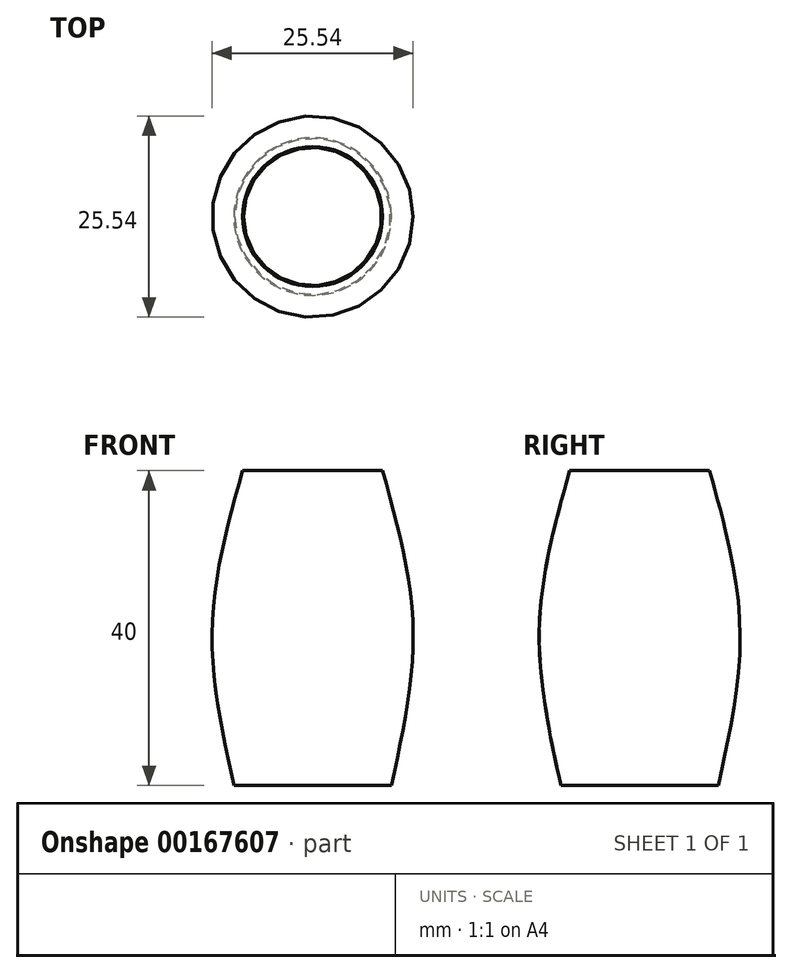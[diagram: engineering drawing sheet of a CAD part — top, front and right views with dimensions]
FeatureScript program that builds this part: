
annotation { "Feature Type Name" : "Feature", "Feature Type Description" : "" }
export const myFeature = defineFeature(function(context is Context, id is Id, definition is map)
    precondition{}
    {
        {
            var Q0;
            Q0=qCreatedBy(makeId("Top.planeOp"),FACE);
            cPlane(context, id + "F0", {"entities" : qUnion([Q0]), "cplaneType" : CPlaneType.OFFSET, "offset" : 20 * mm, "width" : 152.4 * mm, "height" : 152.4 * mm});
        }
        {
            var Q0;
            Q0=qCreatedBy(id+"F0.planeOp",FACE);
            cPlane(context, id + "F1", {"entities" : qUnion([Q0]), "cplaneType" : CPlaneType.OFFSET, "offset" : 20 * mm, "width" : 150 * mm, "height" : 150 * mm});
        }
        {
            var Q0;
            Q0=qCreatedBy(id+"F0.planeOp",FACE);
            var sketch = newSketch(context, id + "F2", { "sketchPlane" : qUnion([Q0])});
            skCircle(sketch, "E0", {"center": v(0, 0) * mm, "radius": 12.76 * mm});
            skSolve(sketch);
        }
        {
            var Q0;
            Q0=qCreatedBy(id+"F1.planeOp",FACE);
            var sketch = newSketch(context, id + "F3", { "sketchPlane" : qUnion([Q0])});
            skCircle(sketch, "E1", {"center": v(0, 0) * mm, "radius": 8.88 * mm});
            skSolve(sketch);
        }
        {
            var Q0;
            Q0=qCreatedBy(makeId("Top.planeOp"),FACE);
            var sketch = newSketch(context, id + "F4", { "sketchPlane" : qUnion([Q0])});
            skCircle(sketch, "E2", {"center": v(0, 0) * mm, "radius": 10 * mm});
            skSolve(sketch);
        }
        {
            var Q0;
            Q0=makeQuery(id+"F4.imprint","IMPRINT",FACE,{"disambiguationData":[TD([[makeQuery(id+"F4.imprint","IMPRINT",EDGE,{"derivedFrom":sQuery(id+"F4.wireOp",EDGE,"E2")}),1.0]])]});
            var Q1;
            Q1=makeQuery(id+"F2.imprint","IMPRINT",FACE,{"disambiguationData":[TD([[makeQuery(id+"F2.imprint","IMPRINT",EDGE,{"derivedFrom":sQuery(id+"F2.wireOp",EDGE,"E0")}),1.0]])]});
            var Q2;
            Q2=makeQuery(id+"F3.imprint","IMPRINT",FACE,{"disambiguationData":[TD([[makeQuery(id+"F3.imprint","IMPRINT",EDGE,{"derivedFrom":sQuery(id+"F3.wireOp",EDGE,"E1")}),1.0]])]});
            loft(context, id + "F5", {"sheetProfilesArray" : [{ "sheetProfileEntities" : qUnion([Q0]) }, { "sheetProfileEntities" : qUnion([Q1]) }, { "sheetProfileEntities" : qUnion([Q2]) }]});
        }
        {
            var Q0;
            Q0=makeQuery(id+"F5.opLoft","CAP_FACE",FACE,{"disambiguationData":[OSD([makeQuery(id+"F3.imprint","IMPRINT",FACE,{"disambiguationData":[TD([[makeQuery(id+"F3.imprint","IMPRINT",EDGE,{"derivedFrom":sQuery(id+"F3.wireOp",EDGE,"E1")}),1.0]])]})])],"isStart":true});
            shell(context, id + "F6", {"entities" : qUnion([Q0]), "thickness" : 0.1 * mm});
        }
    });
